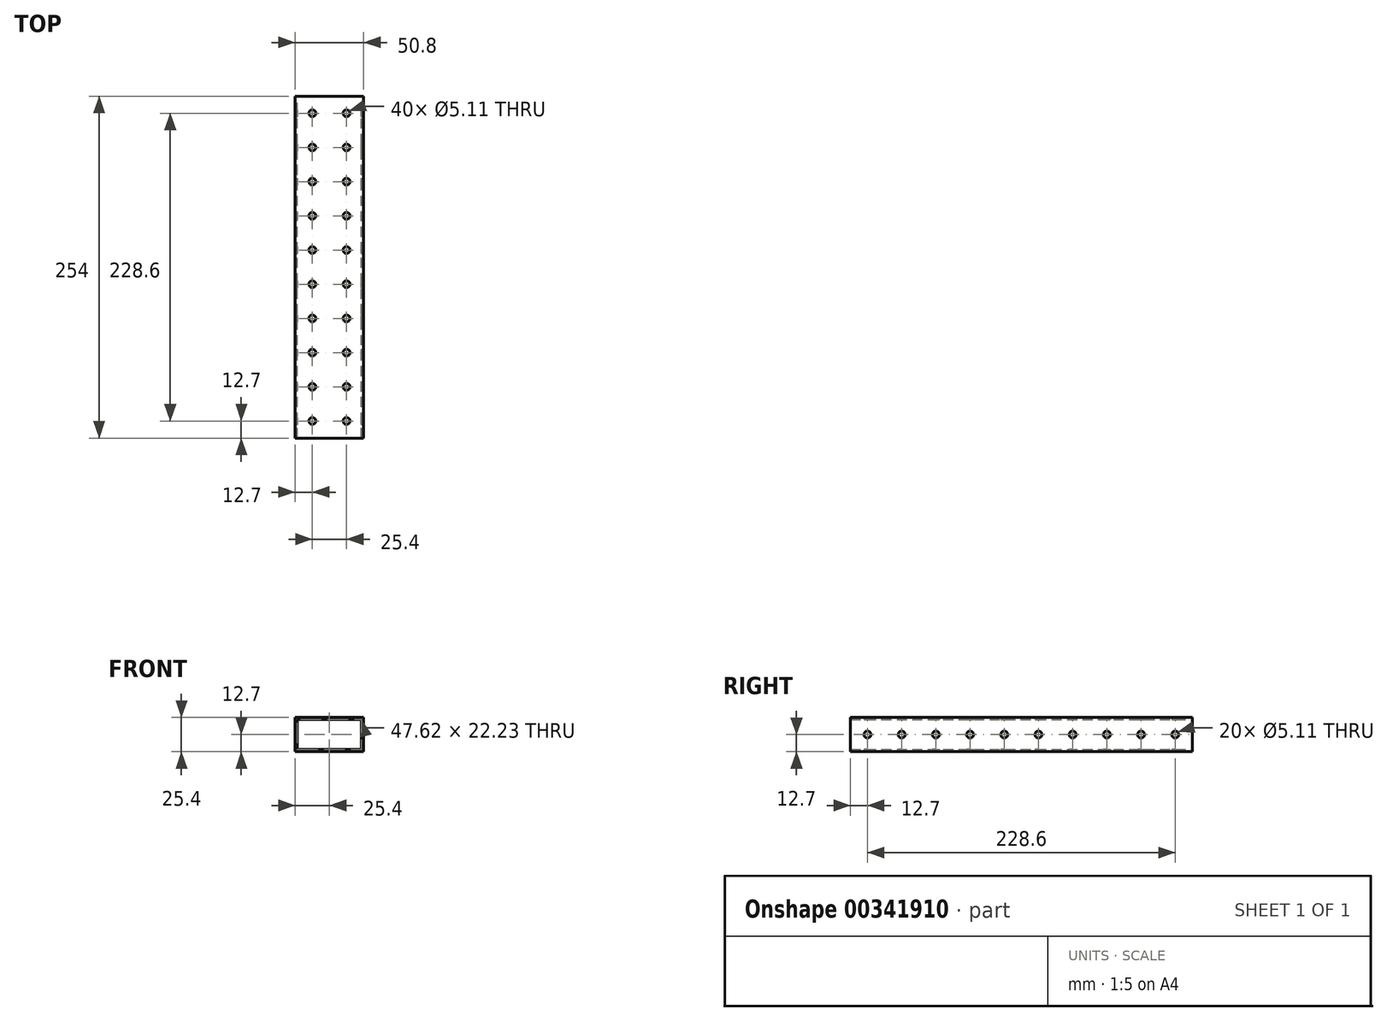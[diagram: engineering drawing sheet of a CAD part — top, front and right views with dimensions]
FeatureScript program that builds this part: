
annotation { "Feature Type Name" : "Feature", "Feature Type Description" : "" }
export const myFeature = defineFeature(function(context is Context, id is Id, definition is map)
    precondition{}
    {
        {
            var Q0;
            Q0=qCreatedBy(makeId("Front.planeOp"),FACE);
            var sketch = newSketch(context, id + "F0", { "sketchPlane" : qUnion([Q0])});
            skLineSegment(sketch, "E0.bottom", {"start": v(-25.4, 12.7) * mm, "end": v(25.4, 12.7) * mm});
            skLineSegment(sketch, "E0.top", {"start": v(-25.4, -12.7) * mm, "end": v(25.4, -12.7) * mm});
            skLineSegment(sketch, "E0.left", {"start": v(-25.4, 12.7) * mm, "end": v(-25.4, -12.7) * mm});
            skLineSegment(sketch, "E0.right", {"start": v(25.4, 12.7) * mm, "end": v(25.4, -12.7) * mm});
            skPoint(sketch, "E0.middle", {"position": v(0, 0) * mm});
            skLineSegment(sketch, "E1.bottom", {"start": v(-23.81, 11.11) * mm, "end": v(23.81, 11.11) * mm});
            skLineSegment(sketch, "E1.top", {"start": v(-23.81, -11.11) * mm, "end": v(23.81, -11.11) * mm});
            skLineSegment(sketch, "E1.left", {"start": v(-23.81, 11.11) * mm, "end": v(-23.81, -11.11) * mm});
            skLineSegment(sketch, "E1.right", {"start": v(23.81, 11.11) * mm, "end": v(23.81, -11.11) * mm});
            skSolve(sketch);
        }
        {
            var Q0;
            Q0=makeQuery(id+"F0.imprint","IMPRINT",FACE,{"disambiguationData":[TD([[makeQuery(id+"F0.imprint","IMPRINT",EDGE,{"derivedFrom":sQuery(id+"F0.wireOp",EDGE,"E0.bottom")}),-1.0]])]});
            extrude(context, id + "F1", {"entities" : qUnion([Q0]), "depth" : 254 * mm});
        }
        {
            var Q0;
            Q0=makeQuery(id+"F1.opExtrude","SWEPT_FACE",FACE,{"disambiguationData":[OSD([sQuery(id+"F0.wireOp",EDGE,"E0.right")])]});
            var sketch = newSketch(context, id + "F2", { "sketchPlane" : qUnion([Q0])});
            skCircle(sketch, "E2", {"center": v(-241.3, 0) * mm, "radius": 2.55 * mm});
            skCircle(sketch, "E3.1.0.0", {"center": v(-215.9, 0) * mm, "radius": 2.55 * mm});
            skCircle(sketch, "E3.2.0.0", {"center": v(-190.5, 0) * mm, "radius": 2.55 * mm});
            skCircle(sketch, "E3.3.0.0", {"center": v(-165.1, 0) * mm, "radius": 2.55 * mm});
            skCircle(sketch, "E3.4.0.0", {"center": v(-139.7, 0) * mm, "radius": 2.55 * mm});
            skCircle(sketch, "E3.5.0.0", {"center": v(-114.3, 0) * mm, "radius": 2.55 * mm});
            skCircle(sketch, "E3.6.0.0", {"center": v(-88.9, 0) * mm, "radius": 2.55 * mm});
            skCircle(sketch, "E3.7.0.0", {"center": v(-63.5, 0) * mm, "radius": 2.55 * mm});
            skCircle(sketch, "E3.8.0.0", {"center": v(-38.1, 0) * mm, "radius": 2.55 * mm});
            skLineSegment(sketch, "E3.direction1", {"start": v(-241.3, 0) * mm, "end": v(-215.9, 0) * mm, "construction": true});
            skCircle(sketch, "E4.0.9.0", {"center": v(-12.7, 0) * mm, "radius": 2.55 * mm});
            skSolve(sketch);
        }
        {
            var Q0;
            Q0=sQuery(id+"F2.wireOp",VERTEX,"E4.0.9.0.center");
            var Q1;
            Q1=sQuery(id+"F2.wireOp",VERTEX,"E3.8.0.0.center");
            var Q2;
            Q2=sQuery(id+"F2.wireOp",VERTEX,"E3.7.0.0.center");
            var Q3;
            Q3=sQuery(id+"F2.wireOp",VERTEX,"E3.6.0.0.center");
            var Q4;
            Q4=sQuery(id+"F2.wireOp",VERTEX,"E3.5.0.0.center");
            var Q5;
            Q5=sQuery(id+"F2.wireOp",VERTEX,"E3.direction1.start");
            var Q6;
            Q6=sQuery(id+"F2.wireOp",VERTEX,"E3.4.0.0.center");
            var Q7;
            Q7=sQuery(id+"F2.wireOp",VERTEX,"E3.3.0.0.center");
            var Q8;
            Q8=sQuery(id+"F2.wireOp",VERTEX,"E3.2.0.0.center");
            var Q9;
            Q9=sQuery(id+"F2.wireOp",VERTEX,"E3.1.0.0.center");
            var Q10;
            Q10=makeQuery(id+"F1.opExtrude","SWEPT_BODY",BODY,{"disambiguationData":[OSD([sQuery(id+"F0.wireOp",EDGE,"E0.bottom"),sQuery(id+"F0.wireOp",EDGE,"E0.top"),sQuery(id+"F0.wireOp",EDGE,"E0.left"),sQuery(id+"F0.wireOp",EDGE,"E0.right"),sQuery(id+"F0.wireOp",EDGE,"E1.bottom"),sQuery(id+"F0.wireOp",EDGE,"E1.top"),sQuery(id+"F0.wireOp",EDGE,"E1.left"),sQuery(id+"F0.wireOp",EDGE,"E1.right")])]});
            hole(context, id + "F3", {"style" : HoleStyle.SIMPLE, "endStyle" : HoleEndStyle.THROUGH, "holeDiameter" : 5.1 * mm, "isTappedThrough" : true, "tappedDepth" : 12.7 * mm, "tapClearance" : 3, "locations" : qUnion([Q0, Q1, Q2, Q3, Q4, Q5, Q6, Q7, Q8, Q9]), "scope" : qUnion([Q10])});
        }
        {
            var Q0;
            Q0=makeQuery(id+"F1.opExtrude","SWEPT_FACE",FACE,{"disambiguationData":[OSD([sQuery(id+"F0.wireOp",EDGE,"E0.top")])]});
            var sketch = newSketch(context, id + "F4", { "sketchPlane" : qUnion([Q0])});
            skCircle(sketch, "E5", {"center": v(-12.7, 12.7) * mm, "radius": 2.55 * mm});
            skCircle(sketch, "E6.0.1.0", {"center": v(-12.7, 38.1) * mm, "radius": 2.55 * mm});
            skCircle(sketch, "E6.0.2.0", {"center": v(-12.7, 63.5) * mm, "radius": 2.55 * mm});
            skCircle(sketch, "E6.0.3.0", {"center": v(-12.7, 88.9) * mm, "radius": 2.55 * mm});
            skCircle(sketch, "E6.0.4.0", {"center": v(-12.7, 114.3) * mm, "radius": 2.55 * mm});
            skCircle(sketch, "E6.0.5.0", {"center": v(-12.7, 139.7) * mm, "radius": 2.55 * mm});
            skCircle(sketch, "E6.0.6.0", {"center": v(-12.7, 165.1) * mm, "radius": 2.55 * mm});
            skCircle(sketch, "E6.0.7.0", {"center": v(-12.7, 190.5) * mm, "radius": 2.55 * mm});
            skCircle(sketch, "E6.0.8.0", {"center": v(-12.7, 215.9) * mm, "radius": 2.55 * mm});
            skCircle(sketch, "E6.0.9.0", {"center": v(-12.7, 241.3) * mm, "radius": 2.55 * mm});
            skCircle(sketch, "E6.1.0.0", {"center": v(12.7, 12.7) * mm, "radius": 2.55 * mm});
            skCircle(sketch, "E6.1.1.0", {"center": v(12.7, 38.1) * mm, "radius": 2.55 * mm});
            skCircle(sketch, "E6.1.2.0", {"center": v(12.7, 63.5) * mm, "radius": 2.55 * mm});
            skCircle(sketch, "E6.1.3.0", {"center": v(12.7, 88.9) * mm, "radius": 2.55 * mm});
            skCircle(sketch, "E6.1.4.0", {"center": v(12.7, 114.3) * mm, "radius": 2.55 * mm});
            skCircle(sketch, "E6.1.5.0", {"center": v(12.7, 139.7) * mm, "radius": 2.55 * mm});
            skCircle(sketch, "E6.1.6.0", {"center": v(12.7, 165.1) * mm, "radius": 2.55 * mm});
            skCircle(sketch, "E6.1.7.0", {"center": v(12.7, 190.5) * mm, "radius": 2.55 * mm});
            skCircle(sketch, "E6.1.8.0", {"center": v(12.7, 215.9) * mm, "radius": 2.55 * mm});
            skCircle(sketch, "E6.1.9.0", {"center": v(12.7, 241.3) * mm, "radius": 2.55 * mm});
            skLineSegment(sketch, "E6.direction1", {"start": v(-12.7, 12.7) * mm, "end": v(12.7, 12.7) * mm, "construction": true});
            skLineSegment(sketch, "E6.direction2", {"start": v(-12.7, 12.7) * mm, "end": v(-12.7, 38.1) * mm, "construction": true});
            skSolve(sketch);
        }
        {
            var Q0;
            Q0=sQuery(id+"F4.wireOp",VERTEX,"E6.0.2.0.center");
            var Q1;
            Q1=sQuery(id+"F4.wireOp",VERTEX,"E6.0.3.0.center");
            var Q2;
            Q2=sQuery(id+"F4.wireOp",VERTEX,"E6.0.4.0.center");
            var Q3;
            Q3=sQuery(id+"F4.wireOp",VERTEX,"E6.0.5.0.center");
            var Q4;
            Q4=sQuery(id+"F4.wireOp",VERTEX,"E6.0.6.0.center");
            var Q5;
            Q5=sQuery(id+"F4.wireOp",VERTEX,"E6.0.7.0.center");
            var Q6;
            Q6=sQuery(id+"F4.wireOp",VERTEX,"E6.0.8.0.center");
            var Q7;
            Q7=sQuery(id+"F4.wireOp",VERTEX,"E6.1.9.0.center");
            var Q8;
            Q8=sQuery(id+"F4.wireOp",VERTEX,"E6.1.5.0.center");
            var Q9;
            Q9=sQuery(id+"F4.wireOp",VERTEX,"E6.1.3.0.center");
            var Q10;
            Q10=sQuery(id+"F4.wireOp",VERTEX,"E6.1.7.0.center");
            var Q11;
            Q11=sQuery(id+"F4.wireOp",VERTEX,"E6.1.4.0.center");
            var Q12;
            Q12=sQuery(id+"F4.wireOp",VERTEX,"E6.1.2.0.center");
            var Q13;
            Q13=sQuery(id+"F4.wireOp",VERTEX,"E6.0.9.0.center");
            var Q14;
            Q14=sQuery(id+"F4.wireOp",VERTEX,"E6.1.1.0.center");
            var Q15;
            Q15=sQuery(id+"F4.wireOp",VERTEX,"E6.1.8.0.center");
            var Q16;
            Q16=sQuery(id+"F4.wireOp",VERTEX,"E6.direction1.end");
            var Q17;
            Q17=sQuery(id+"F4.wireOp",VERTEX,"E6.direction2.start");
            var Q18;
            Q18=sQuery(id+"F4.wireOp",VERTEX,"E6.1.6.0.center");
            var Q19;
            Q19=sQuery(id+"F4.wireOp",VERTEX,"E6.direction2.end");
            var Q20;
            Q20=makeQuery(id+"F1.opExtrude","SWEPT_BODY",BODY,{"disambiguationData":[OSD([sQuery(id+"F0.wireOp",EDGE,"E0.bottom"),sQuery(id+"F0.wireOp",EDGE,"E0.top"),sQuery(id+"F0.wireOp",EDGE,"E0.left"),sQuery(id+"F0.wireOp",EDGE,"E0.right"),sQuery(id+"F0.wireOp",EDGE,"E1.bottom"),sQuery(id+"F0.wireOp",EDGE,"E1.top"),sQuery(id+"F0.wireOp",EDGE,"E1.left"),sQuery(id+"F0.wireOp",EDGE,"E1.right")])]});
            hole(context, id + "F5", {"style" : HoleStyle.SIMPLE, "endStyle" : HoleEndStyle.THROUGH, "holeDiameter" : 5.1 * mm, "isTappedThrough" : true, "tappedDepth" : 12.7 * mm, "tapClearance" : 3, "locations" : qUnion([Q0, Q1, Q2, Q3, Q4, Q5, Q6, Q7, Q8, Q9, Q10, Q11, Q12, Q13, Q14, Q15, Q16, Q17, Q18, Q19]), "scope" : qUnion([Q20])});
        }
    });
